# Revit family: 359746
name_source: partatom
category: Plumbing Fixtures
revit_build: Autodesk Revit 2013 (Build: 20120221_2030(x64)
units: mm (PartAtom-declared; Revit-internal decimal feet)

## types (1)
- 359746
    Assembly Code = D2090800
    CW Connection = Yes
    Calculation flow rate = DW 0,07 l/s, DWW 0,07 l/s
    HW Connection = Yes
    Manufacturer = FRANKE KITCHEN SYSTEMS (PTY) LTD
    Material = Chromium-plated Brass, Polished
    Minimum flow pressure = 1.0 Bar
    Model = Protronic-S AQUA 130, Hands free Hot and Cold Metering Tap
    Product Code = 359746
    Specification = Protronic-S mains-independent, opto-electronically-controlled washbasin mixer DN15 with theft-proof aerator with integrated flow rate regulator. Wash Basin mixer with battery operation.
    Type of Protection = IP 65
    Vent Connection = No
    Volumetric flow = 0.10 l/s at a flow pressure of 3 bar
    Waste Connection = No

## geometry (parser evidence)
native form markers: Blend x4, Sweep x1
no freeform markers — native parametric forms only
